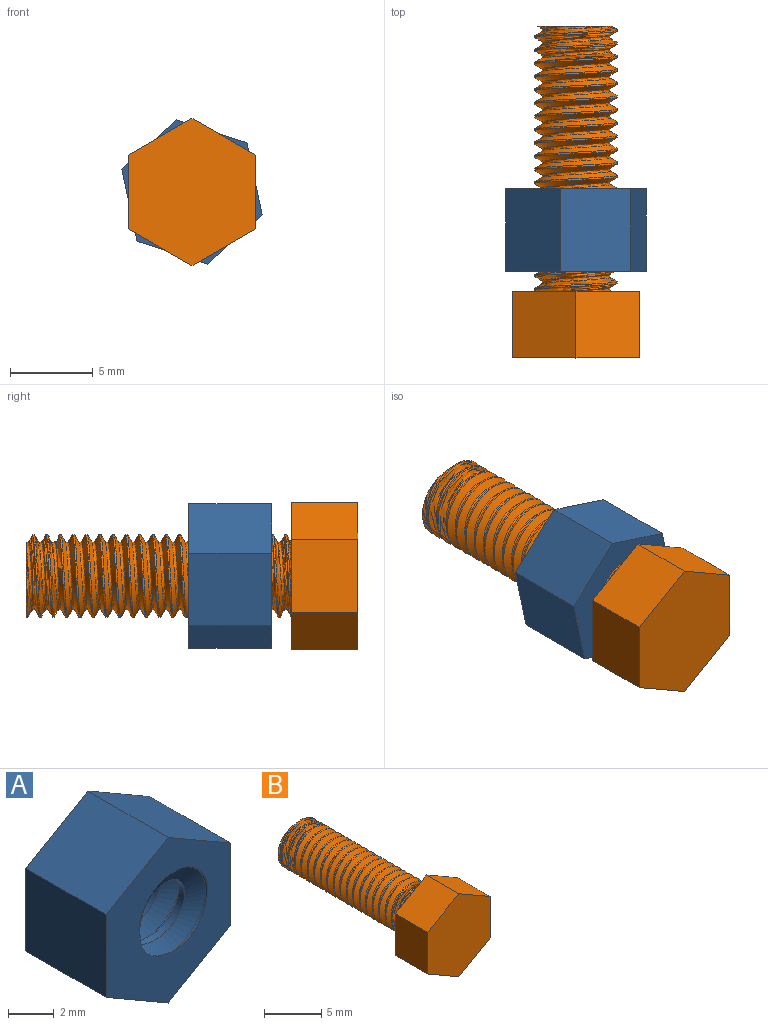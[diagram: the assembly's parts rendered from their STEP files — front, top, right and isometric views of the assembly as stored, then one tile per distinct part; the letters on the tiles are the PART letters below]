
ASSEMBLY  parts=2 mates=1
PART A: 12 faces, bbox 8.1x6.7x9.3 mm
  f0: plane 9.3x8.1mm, normal (0,1,0), area 37.1mm2, adj f2,f3,f4,f5,f6,f7,f8,f9
  f1: plane 9.3x8.1mm, normal (0,-1,0), area 37.1mm2, adj f2,f3,f4,f5,f6,f7,f8,f9
  f2: plane 5x3.85mm, normal (-0.5,0,0.87), area 22.2mm2, adj f0,f1,f3,f7
  f3: plane 5x3.85mm, normal (0.5,0,0.87), area 22.2mm2, adj f0,f1,f2,f4
  f4: plane 5x4.45mm, normal (1,0,0), area 22.2mm2, adj f0,f1,f3,f5
  f5: plane 5x3.85mm, normal (0.5,0,-0.87), area 22.2mm2, adj f0,f1,f4,f6
  f6: plane 5x3.85mm, normal (-0.5,0,-0.87), area 22.2mm2, adj f0,f1,f5,f7
  f7: plane 5x4.45mm, normal (-1,0,0), area 22.2mm2, adj f0,f1,f2,f6
  f8: bspline ~6.22x5.92mm, area 42.4mm2, adj f0,f1,f10,f11
  f9: bspline ~6.22x5.92mm, area 42.5mm2, adj f0,f1,f10,f11
  f10: bspline ~6.07x5.69mm, area 11.8mm2, adj f0,f1,f8,f9
  f11: cylinder r=1.75mm len=5mm, axis (0,1,0), area 13.5mm2, adj f0,f1,f8,f9
PART B: 13 faces, bbox 7.9x20.5x9.1 mm
  f0: cylinder r=2.5mm len=16mm, axis (0,-1,0), area -14.7mm2, adj f1,f9,f11,f12
  f1: plane 4.76x4.73mm, normal (0,1,0), area 16mm2, adj f0,f10,f11,f12
  f2: plane 4x3.85mm, normal (-0.5,0,0.87), area 17.8mm2, adj f3,f7,f8,f9
  f3: plane 4.45x4mm, normal (-1,0,0), area 17.8mm2, adj f2,f4,f8,f9
  f4: plane 4x3.85mm, normal (-0.5,0,-0.87), area 17.8mm2, adj f3,f5,f8,f9
  f5: plane 4x3.85mm, normal (0.5,0,-0.87), area 17.8mm2, adj f4,f6,f8,f9
  f6: plane 4.45x4mm, normal (1,0,0), area 17.8mm2, adj f5,f7,f8,f9
  f7: plane 4x3.85mm, normal (0.5,0,0.87), area 17.8mm2, adj f2,f6,f8,f9
  f8: plane 8.89x7.7mm, normal (0,-1,0), area 51.3mm2, adj f2,f3,f4,f5,f6,f7
  f9: plane 9.11x7.92mm, normal (0,1,0), area 35.4mm2, adj f0,f2,f3,f4,f5,f6,f7,f10
  f10: bspline ~16.6x4.77mm, area 57.7mm2, adj f1,f9,f11,f12
  f11: bspline ~16.65x5.77mm, area 143.8mm2, adj f0,f1,f9,f10
  f12: bspline ~16.52x5.77mm, area 143.1mm2, adj f0,f1,f9,f10
PLACE A rot(axis=(0,1,0),168deg) t=(6.18,9.51,-10.02)mm
PLACE B t=(6.18,8.31,-10.02)mm fixed
MATE cylindrical B.f0 <-> A.f11  axis (0,-1,0) through (6.18,4.31,-10.02)mm
